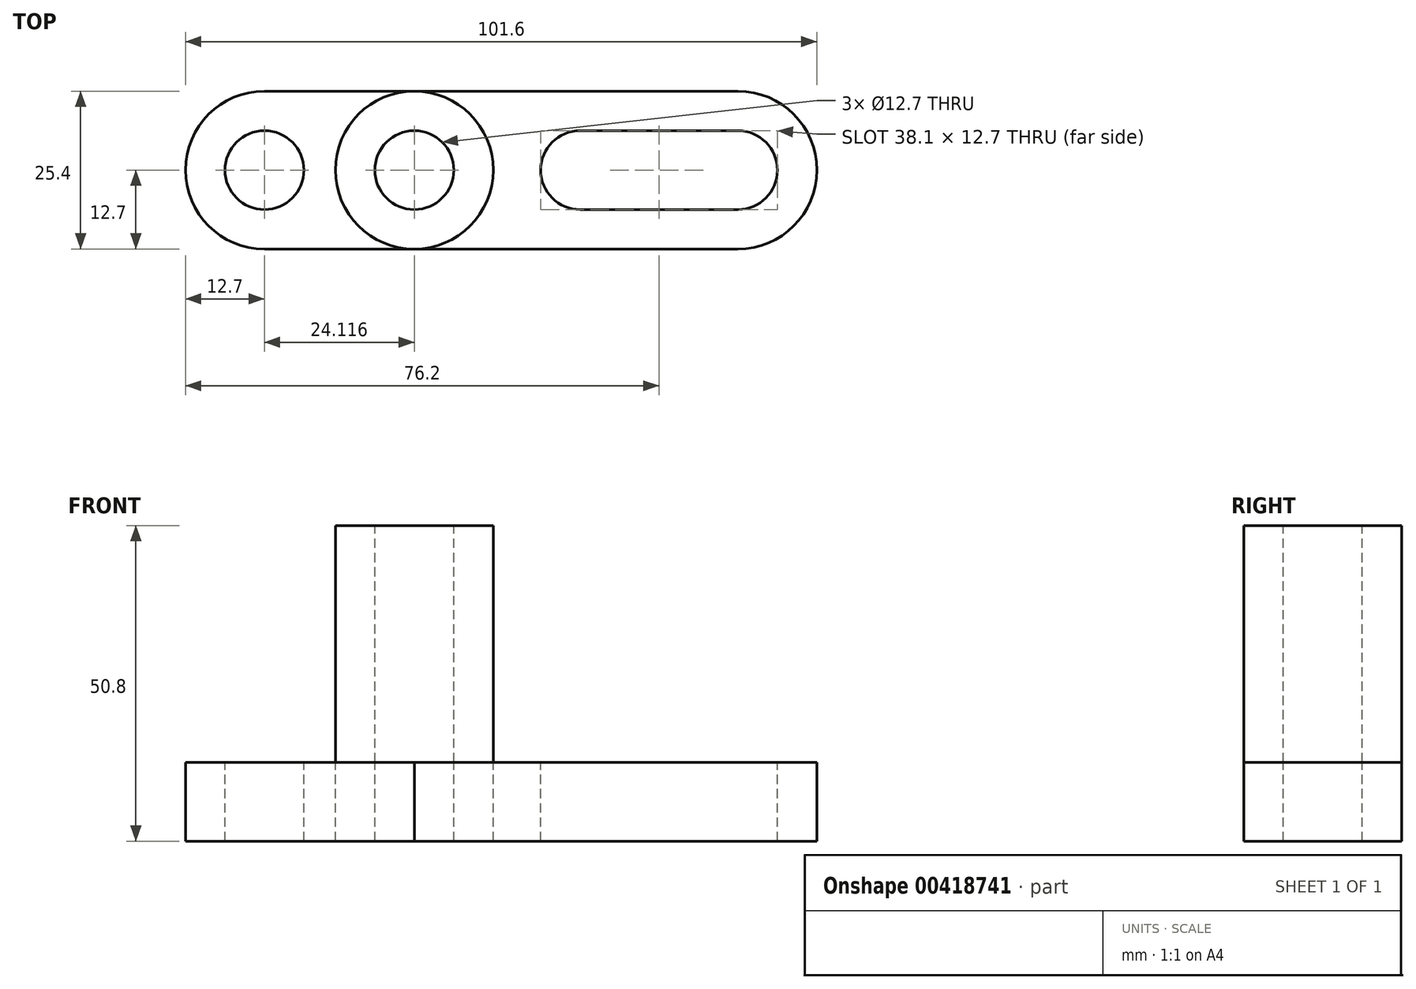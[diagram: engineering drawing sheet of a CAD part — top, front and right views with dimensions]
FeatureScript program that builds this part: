
annotation { "Feature Type Name" : "Feature", "Feature Type Description" : "" }
export const myFeature = defineFeature(function(context is Context, id is Id, definition is map)
    precondition{}
    {
        {
            var Q0;
            Q0=qCreatedBy(makeId("Top.planeOp"),FACE);
            var sketch = newSketch(context, id + "F0", { "sketchPlane" : qUnion([Q0])});
            skLineSegment(sketch, "E0", {"start": v(0, 0) * mm, "end": v(101.6, 0) * mm});
            skLineSegment(sketch, "E1", {"start": v(101.6, 0) * mm, "end": v(101.6, 25.4) * mm});
            skLineSegment(sketch, "E2", {"start": v(101.6, 25.4) * mm, "end": v(0, 25.4) * mm});
            skLineSegment(sketch, "E3", {"start": v(0, 25.4) * mm, "end": v(0, 0) * mm});
            skSolve(sketch);
        }
        {
            var Q0;
            Q0 = qSketchRegion(id + "F0", true);
            extrude(context, id + "F1", {"entities" : qUnion([Q0]), "depth" : 12.7 * mm});
        }
        {
            var Q0;
            Q0=makeQuery(id+"F1.opExtrude","CAP_FACE",FACE,{"disambiguationData":[OSD([sQuery(id+"F0.wireOp",EDGE,"E0"),sQuery(id+"F0.wireOp",EDGE,"E1"),sQuery(id+"F0.wireOp",EDGE,"E2"),sQuery(id+"F0.wireOp",EDGE,"E3")])],"isStart":false});
            var sketch = newSketch(context, id + "F2", { "sketchPlane" : qUnion([Q0])});
            skCircle(sketch, "E4", {"center": v(12.7, 12.7) * mm, "radius": 6.35 * mm});
            skCircle(sketch, "E5", {"center": v(36.82, 12.7) * mm, "radius": 12.7 * mm});
            skSolve(sketch);
        }
        {
            var Q0;
            {var subQ0=sQuery(id+"F2.wireOp",EDGE,"E5");var subQ1=makeQuery(id+"F2.imprint","INTERSECT",VERTEX,{"derivedFrom":[makeQuery(id+"F1.opExtrude","CAP_EDGE",EDGE,{"disambiguationData":[OSD([sQuery(id+"F0.wireOp",EDGE,"E0")])],"isStart":false}),subQ0]});Q0=makeQuery(id+"F2.imprint","IMPRINT",FACE,{"disambiguationData":[TD([[makeQuery(id+"F2.imprint","IMPRINT",EDGE,{"disambiguationData":[TD([[subQ1,1.0]])],"derivedFrom":subQ0}),1.0]])]});}
            extrude(context, id + "F3", {"entities" : qUnion([Q0]), "operationType" : NewBodyOperationType.ADD, "depth" : 38.1 * mm});
        }
        {
            var Q0;
            Q0 = qSketchRegion(id + "F2", true);
            extrude(context, id + "F4", {"entities" : qUnion([Q0]), "operationType" : NewBodyOperationType.REMOVE, "oppositeDirection" : true, "depth" : 25.4 * mm});
        }
        {
            var Q0;
            Q0=makeQuery(id+"F3.opExtrude","CAP_FACE",FACE,{"disambiguationData":[OSD([sQuery(id+"F2.wireOp",EDGE,"E5")])],"isStart":false});
            var sketch = newSketch(context, id + "F5", { "sketchPlane" : qUnion([Q0])});
            skCircle(sketch, "E6", {"center": v(36.82, 12.7) * mm, "radius": 6.35 * mm});
            skSolve(sketch);
        }
        {
            var Q0;
            Q0 = qSketchRegion(id + "F5", true);
            extrude(context, id + "F6", {"entities" : qUnion([Q0]), "operationType" : NewBodyOperationType.REMOVE, "oppositeDirection" : true, "depth" : 50.8 * mm});
        }
        {
            var Q0;
            Q0=makeQuery(id+"F4.boolean.opBoolean","COPY",FACE,{"derivedFrom":makeQuery(id+"F4.opExtrude","CAP_FACE",FACE,{"disambiguationData":[OSD([sQuery(id+"F2.wireOp",EDGE,"E5")])],"isStart":true})});
            extrude(context, id + "F7", {"entities" : qUnion([Q0]), "depth" : 12.7 * mm});
        }
        {
            var Q0;
            {var subQ0=sQuery(id+"F0.wireOp",EDGE,"E2");var subQ1=sQuery(id+"F0.wireOp",EDGE,"E1");var subQ2=sQuery(id+"F0.wireOp",EDGE,"E0");var subQ3=makeQuery(id+"F1.opExtrude","CAP_FACE",FACE,{"disambiguationData":[OSD([subQ2,subQ1,subQ0,sQuery(id+"F0.wireOp",EDGE,"E3")])],"isStart":false});Q0=makeQuery(id+"F3.boolean.opBoolean","SPLIT",FACE,{"disambiguationData":[TD([makeQuery(id+"F1.opExtrude","SWEPT_FACE",FACE,{"disambiguationData":[OSD([subQ1])]})])],"derivedFrom":subQ3});}
            var sketch = newSketch(context, id + "F8", { "sketchPlane" : qUnion([Q0])});
            skCircle(sketch, "E7", {"center": v(63.5, 12.7) * mm, "radius": 6.35 * mm});
            skCircle(sketch, "E8", {"center": v(88.9, 12.7) * mm, "radius": 6.35 * mm});
            skLineSegment(sketch, "E9", {"start": v(63.5, 19.05) * mm, "end": v(88.9, 19.05) * mm});
            skLineSegment(sketch, "E10", {"start": v(63.5, 6.35) * mm, "end": v(88.9, 6.35) * mm});
            skSolve(sketch);
        }
        {
            var Q0;
            Q0 = qSketchRegion(id + "F8", true);
            extrude(context, id + "F9", {"entities" : qUnion([Q0]), "operationType" : NewBodyOperationType.REMOVE, "oppositeDirection" : true, "depth" : 12.7 * mm});
        }
        {
            var Q0;
            {var subQ0=sQuery(id+"F0.wireOp",EDGE,"E2");var subQ1=sQuery(id+"F0.wireOp",EDGE,"E3");var subQ2=sQuery(id+"F0.wireOp",EDGE,"E0");var subQ3=makeQuery(id+"F1.opExtrude","CAP_FACE",FACE,{"disambiguationData":[OSD([subQ2,sQuery(id+"F0.wireOp",EDGE,"E1"),subQ0,subQ1])],"isStart":false});Q0=makeQuery(id+"F3.boolean.opBoolean","SPLIT",FACE,{"disambiguationData":[TD([makeQuery(id+"F1.opExtrude","SWEPT_FACE",FACE,{"disambiguationData":[OSD([subQ1])]})])],"derivedFrom":subQ3});}
            var sketch = newSketch(context, id + "F10", { "sketchPlane" : qUnion([Q0])});
            skArc(sketch, "E11", {"start": v(12.7, 25.4) * mm, "mid": v(0, 12.7) * mm, "end": v(12.7, 0) * mm});
            skSolve(sketch);
        }
        {
            var Q0;
            Q0 = qSketchRegion(id + "F10", true);
            var Q1;
            {var subQ0=sQuery(id+"F10.wireOp",EDGE,"E11");var subQ1=sQuery(id+"F0.wireOp",EDGE,"E3");var subQ5=makeQuery(id+"F1.opExtrude","CAP_EDGE",EDGE,{"disambiguationData":[OSD([subQ1])],"isStart":false});var subQ6=makeQuery(id+"F10.imprint","INTERSECT",VERTEX,{"derivedFrom":[subQ5,subQ0]});Q1=makeQuery(id+"F10.imprint","IMPRINT",FACE,{"disambiguationData":[TD([[makeQuery(id+"F10.imprint","IMPRINT",EDGE,{"disambiguationData":[TD([[subQ6,1.0]])],"derivedFrom":subQ0}),-1.0]])]});}
            var Q2;
            {var subQ0=sQuery(id+"F10.wireOp",EDGE,"E11");var subQ2=sQuery(id+"F0.wireOp",EDGE,"E3");var subQ5=makeQuery(id+"F1.opExtrude","CAP_EDGE",EDGE,{"disambiguationData":[OSD([subQ2])],"isStart":false});var subQ6=makeQuery(id+"F10.imprint","INTERSECT",VERTEX,{"derivedFrom":[subQ5,subQ0]});Q2=makeQuery(id+"F10.imprint","IMPRINT",FACE,{"disambiguationData":[TD([[makeQuery(id+"F10.imprint","IMPRINT",EDGE,{"disambiguationData":[TD([[subQ6,-1.0]])],"derivedFrom":subQ0}),-1.0]])]});}
            extrude(context, id + "F11", {"entities" : qUnion([Q0, Q1, Q2]), "operationType" : NewBodyOperationType.REMOVE, "oppositeDirection" : true, "depth" : 25.4 * mm});
        }
        {
            var Q0;
            {var subQ0=sQuery(id+"F0.wireOp",EDGE,"E2");var subQ1=sQuery(id+"F0.wireOp",EDGE,"E1");var subQ2=sQuery(id+"F0.wireOp",EDGE,"E0");var subQ3=makeQuery(id+"F1.opExtrude","CAP_FACE",FACE,{"disambiguationData":[OSD([subQ2,subQ1,subQ0,sQuery(id+"F0.wireOp",EDGE,"E3")])],"isStart":false});Q0=makeQuery(id+"F3.boolean.opBoolean","SPLIT",FACE,{"disambiguationData":[TD([makeQuery(id+"F1.opExtrude","SWEPT_FACE",FACE,{"disambiguationData":[OSD([subQ1])]})])],"derivedFrom":subQ3});}
            var sketch = newSketch(context, id + "F12", { "sketchPlane" : qUnion([Q0])});
            skArc(sketch, "E12", {"start": v(88.9, 0) * mm, "mid": v(101.6, 12.7) * mm, "end": v(88.9, 25.4) * mm});
            skSolve(sketch);
        }
        {
            var Q0;
            Q0 = qSketchRegion(id + "F12", true);
            var Q1;
            {var subQ0=sQuery(id+"F12.wireOp",EDGE,"E12");var subQ2=sQuery(id+"F0.wireOp",EDGE,"E1");var subQ5=makeQuery(id+"F1.opExtrude","CAP_EDGE",EDGE,{"disambiguationData":[OSD([subQ2])],"isStart":false});var subQ6=makeQuery(id+"F12.imprint","INTERSECT",VERTEX,{"derivedFrom":[subQ5,subQ0]});Q1=makeQuery(id+"F12.imprint","IMPRINT",FACE,{"disambiguationData":[TD([[makeQuery(id+"F12.imprint","IMPRINT",EDGE,{"disambiguationData":[TD([[subQ6,-1.0]])],"derivedFrom":subQ0}),-1.0]])]});}
            var Q2;
            {var subQ0=sQuery(id+"F12.wireOp",EDGE,"E12");var subQ2=sQuery(id+"F0.wireOp",EDGE,"E1");var subQ5=makeQuery(id+"F1.opExtrude","CAP_EDGE",EDGE,{"disambiguationData":[OSD([subQ2])],"isStart":false});var subQ6=makeQuery(id+"F12.imprint","INTERSECT",VERTEX,{"derivedFrom":[subQ5,subQ0]});Q2=makeQuery(id+"F12.imprint","IMPRINT",FACE,{"disambiguationData":[TD([[makeQuery(id+"F12.imprint","IMPRINT",EDGE,{"disambiguationData":[TD([[subQ6,1.0]])],"derivedFrom":subQ0}),-1.0]])]});}
            extrude(context, id + "F13", {"entities" : qUnion([Q0, Q1, Q2]), "operationType" : NewBodyOperationType.REMOVE, "oppositeDirection" : true, "depth" : 25.4 * mm});
        }
    });
